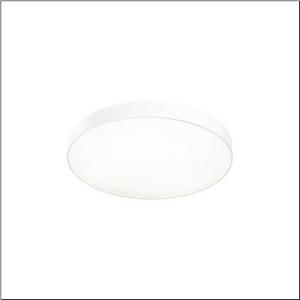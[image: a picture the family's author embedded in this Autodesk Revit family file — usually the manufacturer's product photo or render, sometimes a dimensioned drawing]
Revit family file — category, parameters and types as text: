
# Revit family: round_21_m_51mr36fm8421w
name_source: partatom
category: Lighting Fixtures
units: mm (PartAtom-declared; Revit-internal decimal feet)

## family parameters
Cut with Voids When Loaded = No
Host = Face
Light Source = No
Part Type = Normal
Room Calculation Point = No
Round Connector Dimension = Use Diameter
Shared = No

## types (1)
- --- (1 x LED, 8900 lm, 62.6 W, 4000K)
    Apparent Load = 63 VA
    CIE Flux Codes = 49 80 96 100 100
    Color Rendering = 80
    Color Temperature = 4000K
    Default Elevation = 1800 mm
    Description = Round 21 M, wall and ceiling luminaire, primary optical cover: cover, of PMMA, opal, light emission: direct distribution, primary light characteristic: symmetric, installation type: surface-mounted, suspended mounting, LED, rated luminous flux: 8.140lm, luminous efficacy: 133lm/W, light colour: 840, colour temperature: 4000K, control gear: ON/OFF Multilumen, with terminal, 3-pole, mains connection: 230V, AC, 50/60Hz, rated input power: 61W, housing, of aluminium, coated, white, diameter: 600mm, height: 62mm, protection rating (complete): IP40, insulation class (complete): insulation class I (protective earthing), certification: CE, impact resistance: IK04, permissible operating ambient temperature: -10..+35°C, packaging unit: 1 piece
    Height = 87 mm
    Lamp = 1 x LED
    Lamp Light Flux = 8900 lm
    Lamp Power = 62.6 W
    Lamp count = 1
    Length = 600 mm
    Luminous efficacy = 142 lm/W
    Manufacturer = Siteco
    ModVariant = No
    Model = 51MR36FM8421W
    Mounting Place = Ceiling
    Mounting Type = Surface mounted
    Number of Poles = 1
    OnlyDefault = Yes
    Power Factor = 1
    Product Name = Round 21 M
    Product group = wall and ceiling luminaire
    ProductGroupID = 304
    Protection Class = Protection class I
    Protection Degree = IP 40
    RLX_Detail_Level = 1
    RLX_Emergency_Light_Flux = 0 lm
    RLX_Emergency_Type = 0
    RLX_Emergency_Type_DB = No
    RlxData = <blob elided: 14405 chars, md5=3a586977>
    Socket = socket
    Standby Power = 0 W
    System Light Flux = 8900 lm
    System Power = 63 W
    Type Comments = factory setting: luminous flux: 100 % | (ON | ON | ON | ON) | 700 mA
    Type Image = l_1258330.jpg
    URL = http://relux.com
    VarID = @adj_032942
    Voltage = 0 V
    Weight = 0.00 kg
    Width = 0 mm  [stored 0 ft]

note: [stored X ft] marks values corroborated as IEEE doubles in the binary element streams (Revit-internal decimal feet)

## geometry (parser evidence)
native form markers: Sweep x12
no freeform markers — native parametric forms only
